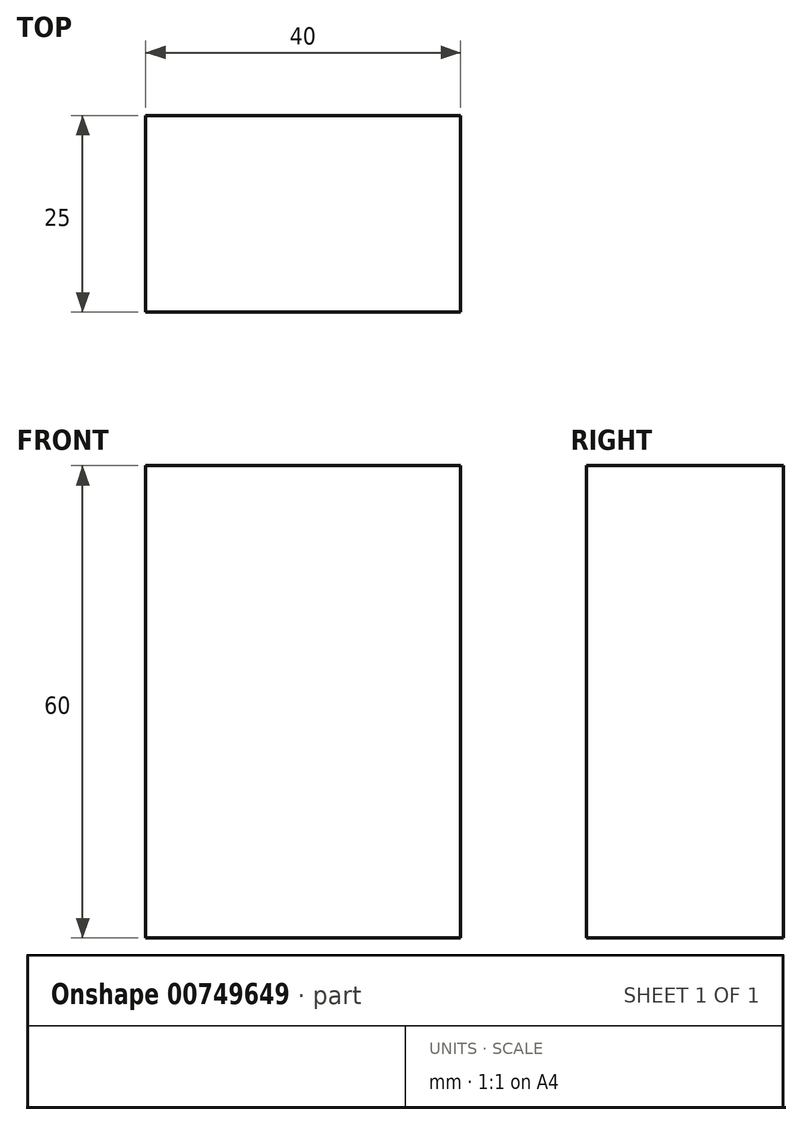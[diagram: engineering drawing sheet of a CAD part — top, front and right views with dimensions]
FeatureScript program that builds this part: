
annotation { "Feature Type Name" : "Feature", "Feature Type Description" : "" }
export const myFeature = defineFeature(function(context is Context, id is Id, definition is map)
    precondition{}
    {
        {
            var Q0;
            Q0=qCreatedBy(makeId("Front.planeOp"),FACE);
            var sketch = newSketch(context, id + "F0", { "sketchPlane" : qUnion([Q0])});
            skLineSegment(sketch, "E0.bottom", {"start": v(0, 0) * mm, "end": v(-40, 0) * mm});
            skLineSegment(sketch, "E0.top", {"start": v(0, -60) * mm, "end": v(-40, -60) * mm});
            skLineSegment(sketch, "E0.left", {"start": v(0, 0) * mm, "end": v(0, -60) * mm});
            skLineSegment(sketch, "E0.right", {"start": v(-40, 0) * mm, "end": v(-40, -60) * mm});
            skSolve(sketch);
        }
        {
            var Q0;
            Q0 = qSketchRegion(id + "F0", true);
            extrude(context, id + "F1", {"entities" : qUnion([Q0]), "depth" : 25 * mm, "offsetDistance" : 25 * mm});
        }
    });
